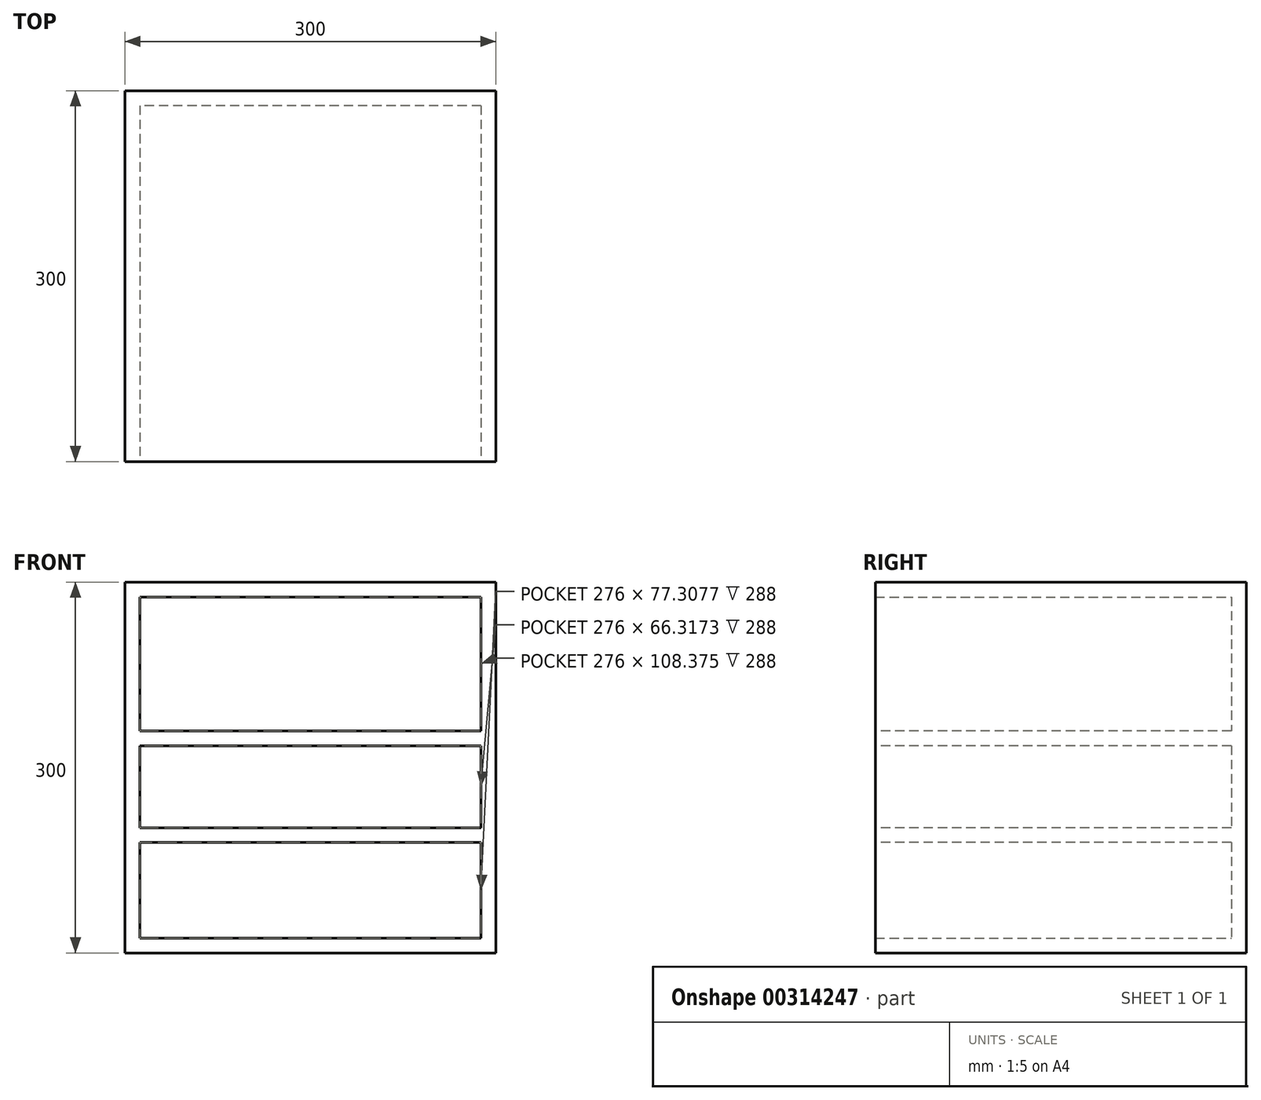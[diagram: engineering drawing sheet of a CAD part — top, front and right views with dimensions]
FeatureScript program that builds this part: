
annotation { "Feature Type Name" : "Feature", "Feature Type Description" : "" }
export const myFeature = defineFeature(function(context is Context, id is Id, definition is map)
    precondition{}
    {
        {
            var Q0;
            Q0=qCreatedBy(makeId("Front.planeOp"),FACE);
            var sketch = newSketch(context, id + "F0", { "sketchPlane" : qUnion([Q0])});
            skLineSegment(sketch, "E0.bottom", {"start": v(150, 150) * mm, "end": v(-150, 150) * mm});
            skLineSegment(sketch, "E0.top", {"start": v(150, -150) * mm, "end": v(-150, -150) * mm});
            skLineSegment(sketch, "E0.left", {"start": v(150, 150) * mm, "end": v(150, -150) * mm});
            skLineSegment(sketch, "E0.right", {"start": v(-150, 150) * mm, "end": v(-150, -150) * mm});
            skPoint(sketch, "E0.middle", {"position": v(0, 0) * mm});
            skSolve(sketch);
        }
        {
            var Q0;
            Q0=makeQuery(id+"F0.imprint","IMPRINT",FACE,{"disambiguationData":[TD([[makeQuery(id+"F0.imprint","IMPRINT",EDGE,{"derivedFrom":sQuery(id+"F0.wireOp",EDGE,"E0.bottom")}),1.0]])]});
            extrude(context, id + "F1", {"entities" : qUnion([Q0]), "endBound" : BoundingType.SYMMETRIC, "depth" : 300 * mm});
        }
        {
            var Q0;
            Q0=makeQuery(id+"F1.opExtrude","CAP_FACE",FACE,{"disambiguationData":[OSD([sQuery(id+"F0.wireOp",EDGE,"E0.bottom"),sQuery(id+"F0.wireOp",EDGE,"E0.top"),sQuery(id+"F0.wireOp",EDGE,"E0.left"),sQuery(id+"F0.wireOp",EDGE,"E0.right")])],"isStart":false});
            shell(context, id + "F2", {"entities" : qUnion([Q0]), "thickness" : 12 * mm});
        }
        {
            var Q0;
            Q0=makeQuery(id+"F1.opExtrude","CAP_FACE",FACE,{"disambiguationData":[OSD([sQuery(id+"F0.wireOp",EDGE,"E0.bottom"),sQuery(id+"F0.wireOp",EDGE,"E0.top"),sQuery(id+"F0.wireOp",EDGE,"E0.left"),sQuery(id+"F0.wireOp",EDGE,"E0.right")])],"isStart":false});
            var sketch = newSketch(context, id + "F3", { "sketchPlane" : qUnion([Q0])});
            skLineSegment(sketch, "E1.bottom", {"start": v(144, 29.62) * mm, "end": v(-144, 29.62) * mm});
            skLineSegment(sketch, "E1.top", {"start": v(144, 17.62) * mm, "end": v(-144, 17.62) * mm});
            skLineSegment(sketch, "E1.left", {"start": v(144, 29.62) * mm, "end": v(144, 17.62) * mm});
            skLineSegment(sketch, "E1.right", {"start": v(-144, 29.62) * mm, "end": v(-144, 17.62) * mm});
            skPoint(sketch, "E1.middle", {"position": v(0, 23.62) * mm});
            skSolve(sketch);
        }
        {
            var Q0;
            {var subQ0=sQuery(id+"F3.wireOp",EDGE,"E1.bottom");var subQ1=sQuery(id+"F0.wireOp",EDGE,"E0.left");var subQ2=makeQuery(id+"F2.opShell","OFFSET_EDGE",EDGE,{"disambiguationData":[OSD([subQ1]),TDD([makeQuery(id+"F1.opExtrude","CAP_EDGE",EDGE,{"disambiguationData":[OSD([subQ1])],"isStart":false})])]});var subQ3=makeQuery(id+"F3.imprint","INTERSECT",VERTEX,{"derivedFrom":[subQ2,subQ0]});Q0=makeQuery(id+"F3.imprint","IMPRINT",FACE,{"disambiguationData":[TD([[makeQuery(id+"F3.imprint","IMPRINT",EDGE,{"disambiguationData":[TD([[subQ3,-1.0]])],"derivedFrom":subQ0}),1.0]])]});}
            extrude(context, id + "F4", {"entities" : qUnion([Q0]), "operationType" : NewBodyOperationType.ADD, "oppositeDirection" : true, "depth" : 288 * mm});
        }
        {
            var Q0;
            {var subQ0=sQuery(id+"F0.wireOp",EDGE,"E0.right");var subQ1=sQuery(id+"F0.wireOp",EDGE,"E0.left");Q0=makeQuery(id+"F4.boolean.opBoolean","MERGE",FACE,{"derivedFrom":[makeQuery(id+"F1.opExtrude","CAP_FACE",FACE,{"disambiguationData":[OSD([sQuery(id+"F0.wireOp",EDGE,"E0.bottom"),sQuery(id+"F0.wireOp",EDGE,"E0.top"),subQ1,subQ0])],"isStart":false}),makeQuery(id+"F4.opExtrude","CAP_FACE",FACE,{"disambiguationData":[OSD([subQ1,subQ0,sQuery(id+"F3.wireOp",EDGE,"E1.bottom"),sQuery(id+"F3.wireOp",EDGE,"E1.top")])],"isStart":true})]});}
            var sketch = newSketch(context, id + "F5", { "sketchPlane" : qUnion([Q0])});
            skLineSegment(sketch, "E2.bottom", {"start": v(145.38, -48.7) * mm, "end": v(-145.38, -48.7) * mm});
            skLineSegment(sketch, "E2.top", {"start": v(145.38, -60.7) * mm, "end": v(-145.38, -60.7) * mm});
            skLineSegment(sketch, "E2.left", {"start": v(145.38, -48.7) * mm, "end": v(145.38, -60.7) * mm});
            skLineSegment(sketch, "E2.right", {"start": v(-145.38, -48.7) * mm, "end": v(-145.38, -60.7) * mm});
            skPoint(sketch, "E2.middle", {"position": v(0, -54.7) * mm});
            skSolve(sketch);
        }
        {
            var Q0;
            {var subQ0=sQuery(id+"F5.wireOp",EDGE,"E2.bottom");var subQ3=sQuery(id+"F0.wireOp",EDGE,"E0.left");var subQ5=sQuery(id+"F0.wireOp",EDGE,"E0.top");var subQ6=makeQuery(id+"F2.opShell","OFFSET_FACE",FACE,{"disambiguationData":[OSD([subQ5])]});var subQ9=makeQuery(id+"F4.boolean.opBoolean","SPLIT",EDGE,{"disambiguationData":[TD([subQ6])],"derivedFrom":makeQuery(id+"F2.opShell","OFFSET_EDGE",EDGE,{"disambiguationData":[OSD([subQ3]),TDD([makeQuery(id+"F1.opExtrude","CAP_EDGE",EDGE,{"disambiguationData":[OSD([subQ3])],"isStart":false})])]})});var subQ10=makeQuery(id+"F5.imprint","INTERSECT",VERTEX,{"derivedFrom":[subQ9,subQ0]});Q0=makeQuery(id+"F5.imprint","IMPRINT",FACE,{"disambiguationData":[TD([[makeQuery(id+"F5.imprint","IMPRINT",EDGE,{"disambiguationData":[TD([[subQ10,-1.0]])],"derivedFrom":subQ0}),1.0]])]});}
            extrude(context, id + "F6", {"entities" : qUnion([Q0]), "operationType" : NewBodyOperationType.ADD, "oppositeDirection" : true, "depth" : 288 * mm});
        }
    });
